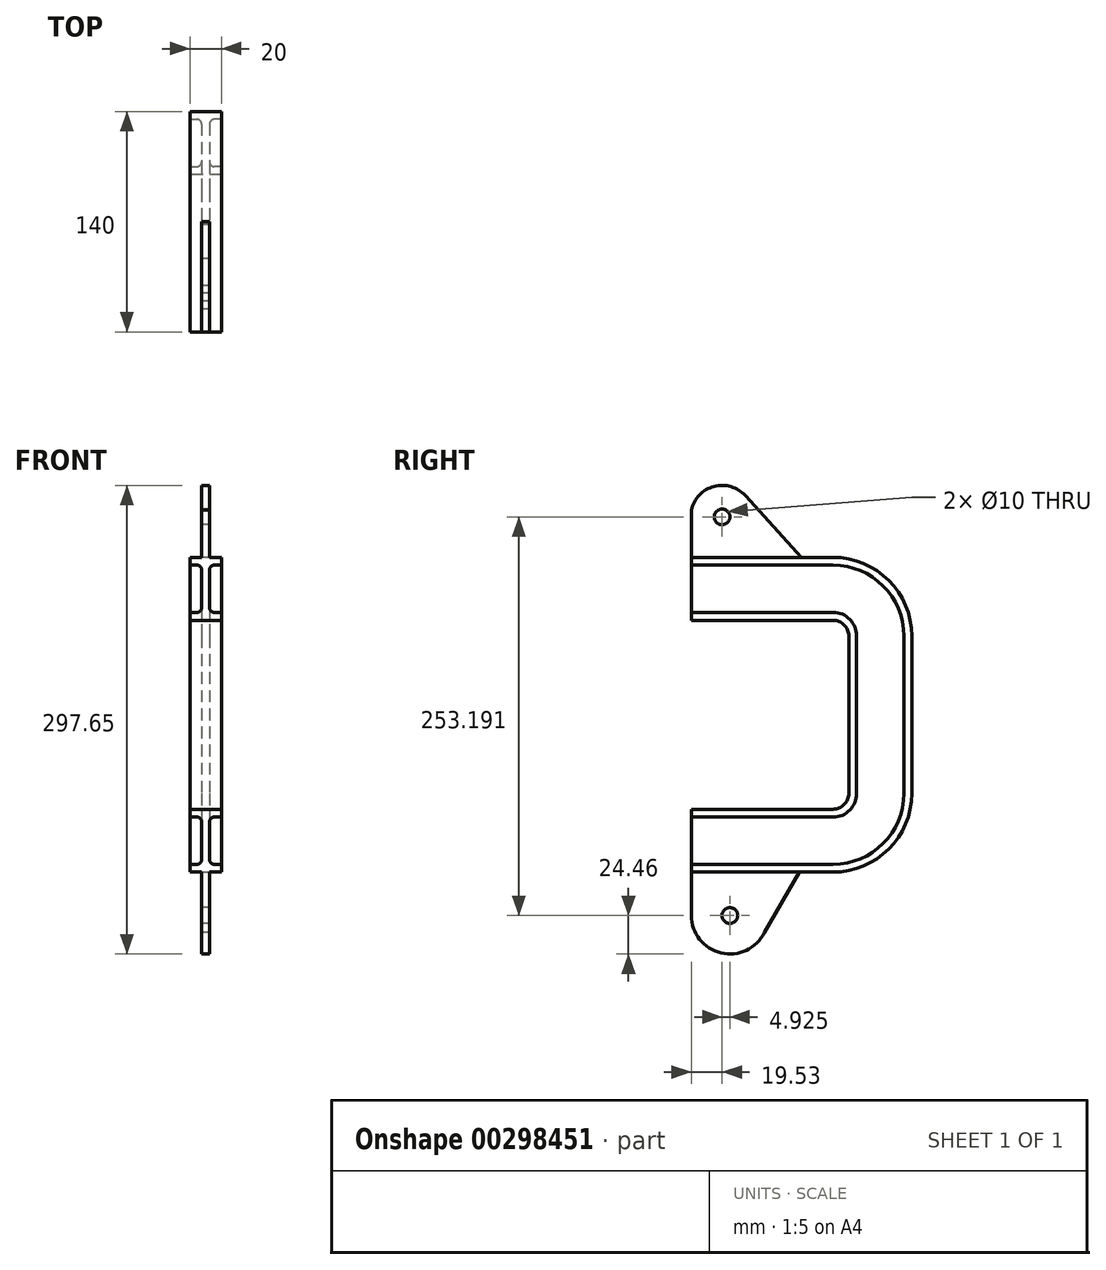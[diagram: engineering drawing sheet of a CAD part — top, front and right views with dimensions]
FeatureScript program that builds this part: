
annotation { "Feature Type Name" : "Feature", "Feature Type Description" : "" }
export const myFeature = defineFeature(function(context is Context, id is Id, definition is map)
    precondition{}
    {
        {
            var Q0;
            Q0=qCreatedBy(makeId("Front.planeOp"),FACE);
            var sketch = newSketch(context, id + "F0", { "sketchPlane" : qUnion([Q0])});
            skLineSegment(sketch, "E0", {"start": v(0, 20) * mm, "end": v(10, 20) * mm});
            skLineSegment(sketch, "E1", {"start": v(10, 20) * mm, "end": v(10, 15) * mm});
            skLineSegment(sketch, "E2", {"start": v(10, 15) * mm, "end": v(5.5, 15) * mm});
            skLineSegment(sketch, "E3", {"start": v(2.5, 12) * mm, "end": v(2.5, 0) * mm});
            skPoint(sketch, "E4.visualSharp", {"position": v(2.5, 15) * mm});
            skArc(sketch, "E4.filletArc", {"start": v(5.5, 15) * mm, "mid": v(3.38, 14.12) * mm, "end": v(2.5, 12) * mm});
            skArc(sketch, "E5.MirrorCS", {"start": v(-5.5, 15) * mm, "mid": v(-3.38, 14.12) * mm, "end": v(-2.5, 12) * mm});
            skLineSegment(sketch, "E6.MirrorCS", {"start": v(0, 20) * mm, "end": v(-10, 20) * mm});
            skLineSegment(sketch, "E7.MirrorCS", {"start": v(-10, 20) * mm, "end": v(-10, 15) * mm});
            skPoint(sketch, "E8.MirrorP", {"position": v(-2.5, 15) * mm});
            skLineSegment(sketch, "E9.MirrorCS", {"start": v(-10, 15) * mm, "end": v(-5.5, 15) * mm});
            skLineSegment(sketch, "E10.MirrorCS", {"start": v(-2.5, 12) * mm, "end": v(-2.5, 0) * mm});
            skArc(sketch, "E11.MirrorCS", {"start": v(-5.5, -15) * mm, "mid": v(-3.38, -14.12) * mm, "end": v(-2.5, -12) * mm});
            skArc(sketch, "E12.MirrorCS", {"start": v(5.5, -15) * mm, "mid": v(3.38, -14.12) * mm, "end": v(2.5, -12) * mm});
            skPoint(sketch, "E13.MirrorP", {"position": v(-2.5, -15) * mm});
            skLineSegment(sketch, "E14.MirrorCS", {"start": v(-2.5, -12) * mm, "end": v(-2.5, 0) * mm});
            skLineSegment(sketch, "E15.MirrorCS", {"start": v(-10, -15) * mm, "end": v(-5.5, -15) * mm});
            skLineSegment(sketch, "E16.MirrorCS", {"start": v(-10, -20) * mm, "end": v(-10, -15) * mm});
            skLineSegment(sketch, "E17.MirrorCS", {"start": v(0, -20) * mm, "end": v(-10, -20) * mm});
            skLineSegment(sketch, "E18.MirrorCS", {"start": v(10, -20) * mm, "end": v(10, -15) * mm});
            skLineSegment(sketch, "E19.MirrorCS", {"start": v(10, -15) * mm, "end": v(5.5, -15) * mm});
            skPoint(sketch, "E20.MirrorP", {"position": v(2.5, -15) * mm});
            skLineSegment(sketch, "E21.MirrorCS", {"start": v(0, -20) * mm, "end": v(10, -20) * mm});
            skLineSegment(sketch, "E22.MirrorCS", {"start": v(2.5, -12) * mm, "end": v(2.5, 0) * mm});
            skSolve(sketch);
        }
        {
            var Q0;
            Q0=qCreatedBy(makeId("Right.planeOp"),FACE);
            var sketch = newSketch(context, id + "F1", { "sketchPlane" : qUnion([Q0])});
            skLineSegment(sketch, "E23", {"start": v(0, -20) * mm, "end": v(90, -20) * mm});
            skLineSegment(sketch, "E24", {"start": v(100, -30) * mm, "end": v(100, -70) * mm});
            skPoint(sketch, "E25.visualSharp", {"position": v(100, -20) * mm});
            skArc(sketch, "E25.filletArc", {"start": v(100, -30) * mm, "mid": v(97.07, -22.93) * mm, "end": v(90, -20) * mm});
            skLineSegment(sketch, "E26", {"start": v(100, -70) * mm, "end": v(100, -130) * mm});
            skLineSegment(sketch, "E27", {"start": v(90, -140) * mm, "end": v(0, -140) * mm});
            skPoint(sketch, "E28.visualSharp", {"position": v(100, -140) * mm});
            skArc(sketch, "E28.filletArc", {"start": v(90, -140) * mm, "mid": v(97.07, -137.07) * mm, "end": v(100, -130) * mm});
            skSolve(sketch);
        }
        {
            var Q0;
            Q0 = qSketchRegion(id + "F0", true);
            var Q1;
            Q1 = qConstructionFilter(qBodyType(qCreatedBy(id + "F1" ,EDGE), BodyType.WIRE), ConstructionObject.NO);
            sweep(context, id + "F2", {"profiles" : qUnion([Q0]), "path" : qUnion([Q1])});
        }
        {
            var Q0;
            Q0=qCreatedBy(makeId("Right.planeOp"),FACE);
            var sketch = newSketch(context, id + "F3", { "sketchPlane" : qUnion([Q0])});
            skLineSegment(sketch, "E29", {"start": v(0, 20) * mm, "end": v(70, 20) * mm});
            skLineSegment(sketch, "E30", {"start": v(70, 20) * mm, "end": v(0, 20) * mm});
            skLineSegment(sketch, "E31", {"start": v(0, 20) * mm, "end": v(0, 50) * mm});
            skLineSegment(sketch, "E32", {"start": v(70, 20) * mm, "end": v(34.31, 59.16) * mm});
            skArc(sketch, "E33", {"start": v(34.31, 59.16) * mm, "mid": v(14.37, 65.01) * mm, "end": v(0, 50) * mm});
            skCircle(sketch, "E34", {"center": v(19.53, 45.7) * mm, "radius": 5 * mm});
            skSolve(sketch);
        }
        {
            var Q0;
            Q0 = qSketchRegion(id + "F3", true);
            extrude(context, id + "F4", {"entities" : qUnion([Q0]), "operationType" : NewBodyOperationType.ADD, "endBound" : BoundingType.SYMMETRIC, "depth" : 5 * mm});
        }
        {
            var Q0;
            Q0=qCreatedBy(makeId("Right.planeOp"),FACE);
            var sketch = newSketch(context, id + "F5", { "sketchPlane" : qUnion([Q0])});
            skLineSegment(sketch, "E35", {"start": v(0, -177.5) * mm, "end": v(70, -177.5) * mm});
            skLineSegment(sketch, "E36", {"start": v(70, -177.5) * mm, "end": v(0, -177.5) * mm});
            skLineSegment(sketch, "E37", {"start": v(0, -177.5) * mm, "end": v(0, -207.5) * mm});
            skLineSegment(sketch, "E38", {"start": v(70, -177.5) * mm, "end": v(46.4, -218.3) * mm});
            skArc(sketch, "E39", {"start": v(0, -207.5) * mm, "mid": v(18.91, -231.32) * mm, "end": v(46.4, -218.3) * mm});
            skCircle(sketch, "E40", {"center": v(24.46, -207.5) * mm, "radius": 5 * mm});
            skSolve(sketch);
        }
        {
            var Q0;
            Q0 = qSketchRegion(id + "F5", true);
            extrude(context, id + "F6", {"entities" : qUnion([Q0]), "operationType" : NewBodyOperationType.ADD, "endBound" : BoundingType.SYMMETRIC, "depth" : 5 * mm});
        }
    });
